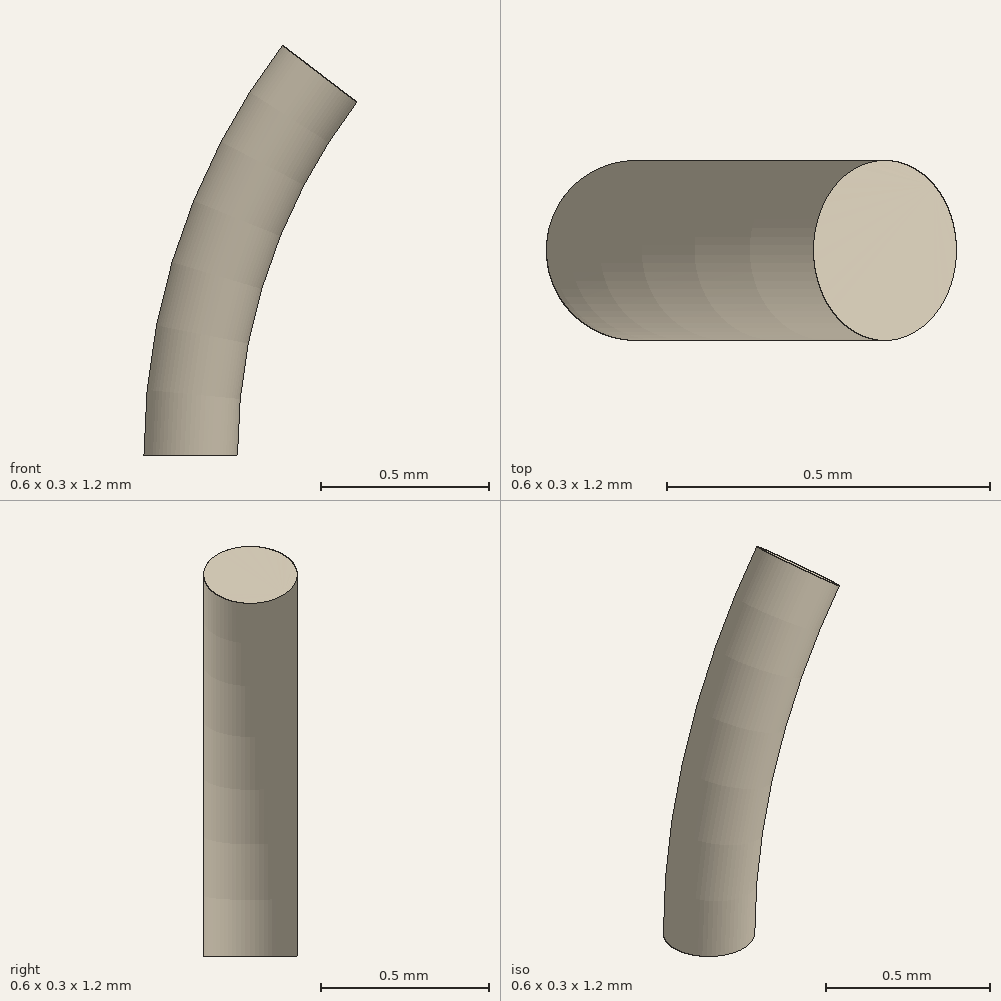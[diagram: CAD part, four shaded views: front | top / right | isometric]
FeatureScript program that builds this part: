
annotation { "Feature Type Name" : "Feature", "Feature Type Description" : "" }
export const myFeature = defineFeature(function(context is Context, id is Id, definition is map)
    precondition{}
    {
        {
            var Q0;
            Q0=qCreatedBy(makeId("Top.planeOp"),FACE);
            var sketch = newSketch(context, id + "F0", { "sketchPlane" : qUnion([Q0])});
            skCircle(sketch, "E0", {"center": v(0, 0) * mm, "radius": 0.14 * mm});
            skSolve(sketch);
        }
        {
            var Q0;
            Q0=qCreatedBy(makeId("Front.planeOp"),FACE);
            var sketch = newSketch(context, id + "F1", { "sketchPlane" : qUnion([Q0])});
            skArc(sketch, "E1", {"start": v(0, 0) * mm, "mid": v(0.1, 0.6) * mm, "end": v(0.39, 1.14) * mm});
            skSolve(sketch);
        }
        {
            var Q0;
            Q0 = qSketchRegion(id + "F0", true);
            var Q1;
            Q1 = qConstructionFilter(qBodyType(qCreatedBy(id + "F1" ,EDGE), BodyType.WIRE), ConstructionObject.NO);
            sweep(context, id + "F2", {"profiles" : qUnion([Q0]), "path" : qUnion([Q1])});
        }
    });
